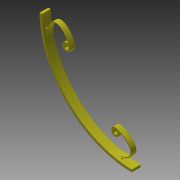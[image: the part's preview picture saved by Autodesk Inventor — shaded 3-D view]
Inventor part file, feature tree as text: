
AUTODESK INVENTOR PART (.ipt)
format: ipt  version: 2015 (Build 190159000, 159)  size: 223,744 bytes
history: native  units: mm
features: extrude x4, sketch x4, fillet x2, other x1
ambient origin geometry x8: Origin, YZ Plane, XZ Plane, XY Plane, X Axis, Y Axis, Z Axis, Center Point
bodies: Body1 (feature_tree)
feature tree (11):
  other  "Sólido1"
  extrude  "Extrusión1"  Depth=300.0mm
  sketch  "Boceto3"  dims[d2=270.0mm d3=10.0mm]
  extrude  "Extrusión3"  Depth=10.0mm
  extrude  "Extrusión4"  Depth=3.0mm
  extrude  "Extrusión5"  Depth=5.0mm
  fillet  "Empalme2"  Radius=3.0mm
  fillet  "Empalme3"  Radius=0.5mm
  sketch  "Boceto1"  dims[d0=292.0mm d1=300.0mm]
  sketch  "Boceto4"  dims[d4=6.0mm d6=3.0mm]
  sketch  "Boceto5"  dims[d7=0.5mm d8=35.0mm d9=3.0mm d10=0.5mm d11=6.0mm d12=35.0mm d14=8.0mm d15=0.0mm d19=1.5mm d20=1.5mm d23=135.0deg d27=0.174533mm d28=0.174533mm d29=8.0mm d30=0.0mm d31=8.0mm d32=0.0mm d33=14.0mm d34=0.0mm d35=1.0mm d36=5.0mm]
